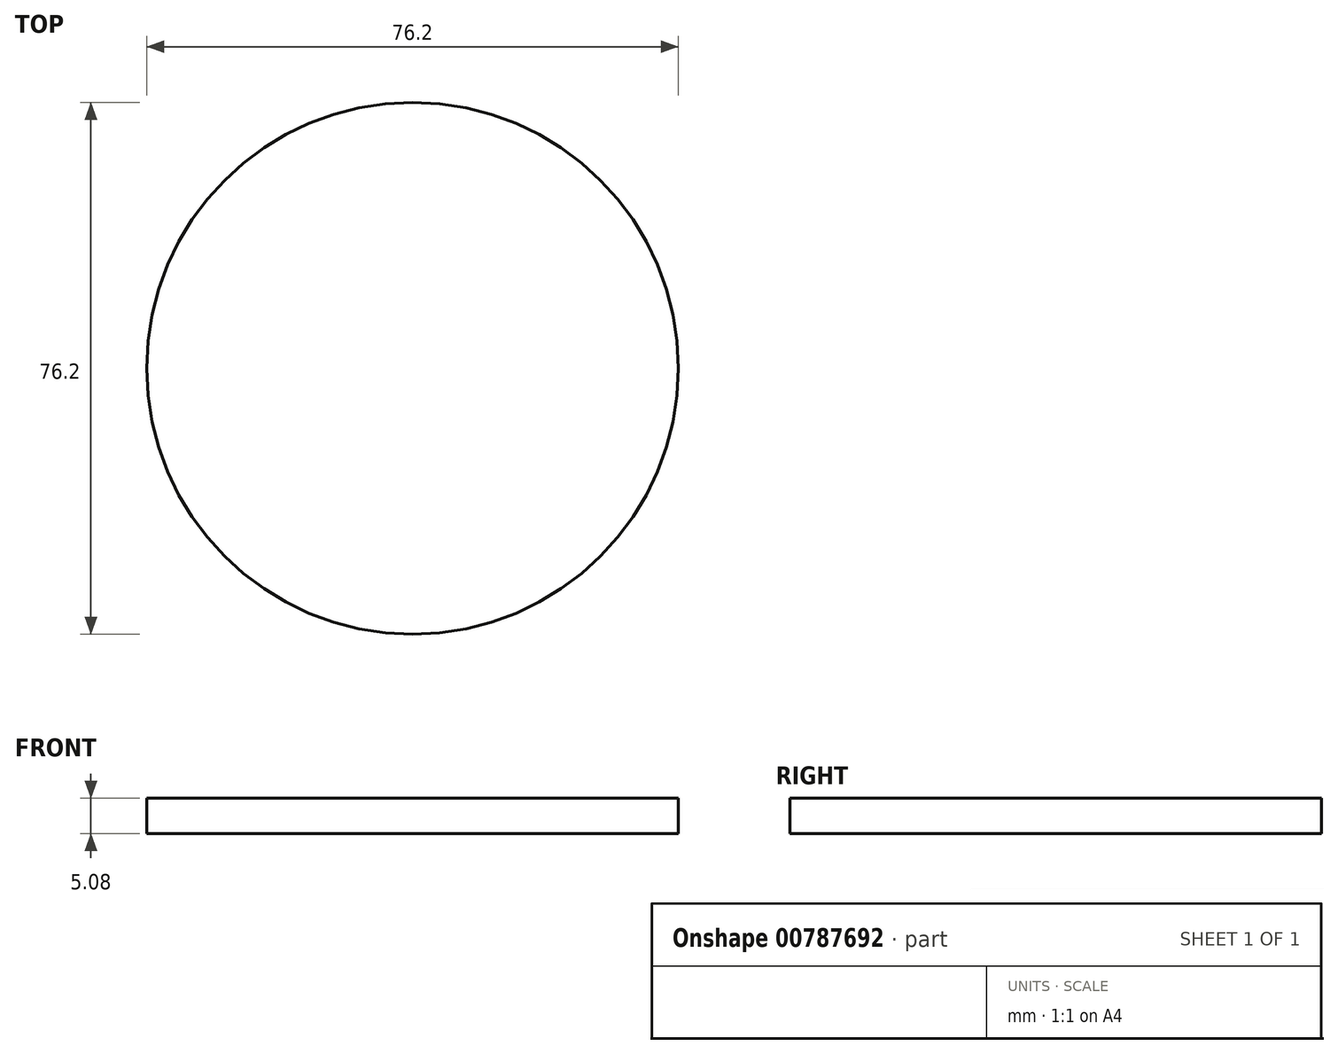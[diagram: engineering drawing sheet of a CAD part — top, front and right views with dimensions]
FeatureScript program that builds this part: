
annotation { "Feature Type Name" : "Feature", "Feature Type Description" : "" }
export const myFeature = defineFeature(function(context is Context, id is Id, definition is map)
    precondition{}
    {
        {
            var Q0;
            Q0=qCreatedBy(makeId("Top.planeOp"),FACE);
            var sketch = newSketch(context, id + "F0", { "sketchPlane" : qUnion([Q0])});
            skCircle(sketch, "E0", {"center": v(0, 0) * mm, "radius": 38.1 * mm});
            skSolve(sketch);
        }
        {
            var Q0;
            Q0=makeQuery(id+"F0.imprint","IMPRINT",FACE,{"disambiguationData":[TD([[makeQuery(id+"F0.imprint","IMPRINT",EDGE,{"derivedFrom":sQuery(id+"F0.wireOp",EDGE,"E0")}),1.0]])]});
            extrude(context, id + "F1", {"entities" : qUnion([Q0]), "depth" : 5.08 * mm, "offsetDistance" : 25.4 * mm});
        }
    });
